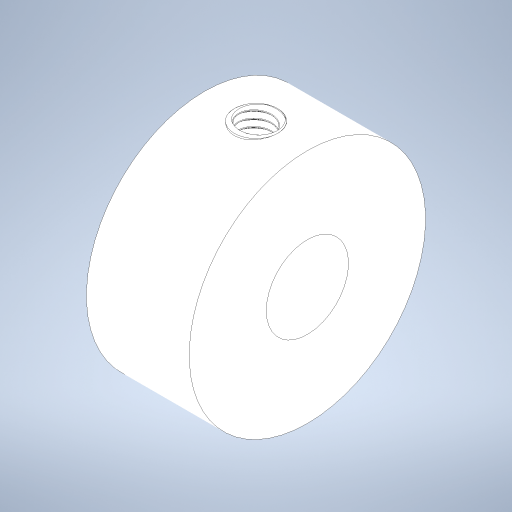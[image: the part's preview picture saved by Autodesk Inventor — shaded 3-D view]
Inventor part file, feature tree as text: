
AUTODESK INVENTOR PART (.ipt)
format: ipt  version: 2023 (Build 270158000, 158)  size: 704,512 bytes
history: native  units: in
note: dims shown in document units (in); Inventor stores cm internally (conversion verified against a paired STEP export)
features: sketch x5, extrude x3, plane x1, thread x1, revolve x1, helix x1
ambient origin geometry x8: Origin, YZ Plane, XZ Plane, XY Plane, X Axis, Y Axis, Z Axis, Center Point
bodies: Solid1 (feature_tree), Solid5 (feature_tree)
feature tree (12):
  extrude  "Extrusion1"  Depth=0.3937in TaperAngle=0.0deg
  plane  "Work Plane1"
  sketch  "Sketch2"  dims[d3=0.4528in d4=0.1654in]
  extrude  "Extrusion2"  Depth=0.4528in
  extrude  "Extrusion3"  Depth=0.3937in TaperAngle=0.0deg
  thread  "Thread4"  [1 undecoded]
  revolve  "Revolution4"  [1 undecoded]
  helix  "Coil4"  [1 undecoded]
  sketch  "Sketch1"  dims[d0=0.9055in d1=0.3937in d2=0.0in]
  sketch  "Sketch5"  dims[d5=0.1969in d6=0.3937in d7=0.0in d17=0.3779in]
  sketch  "Sketch10"  dims[d28=0.315in d29=0.3937in d30=0.0in d40=0.3779in]
  sketch  "Sketch11"  dims[d60=0.3779in d71=0.1969in d72=0.0in d73=0.3779in d74=0.0044in d75=0.0044in d78=0.0276in d80=0.3779in d82=0.0in d83=0.0276in d84=0.252in d85=0.3937in d86=0.0in d87=0.0in d88=0.0in d89=0.0in d90=0.0in]
note: 3 required parameter values undecoded (feature->parameter linkage not recoverable at this tier; creation-order binding heuristic only, values carry confidence <= 0.55)